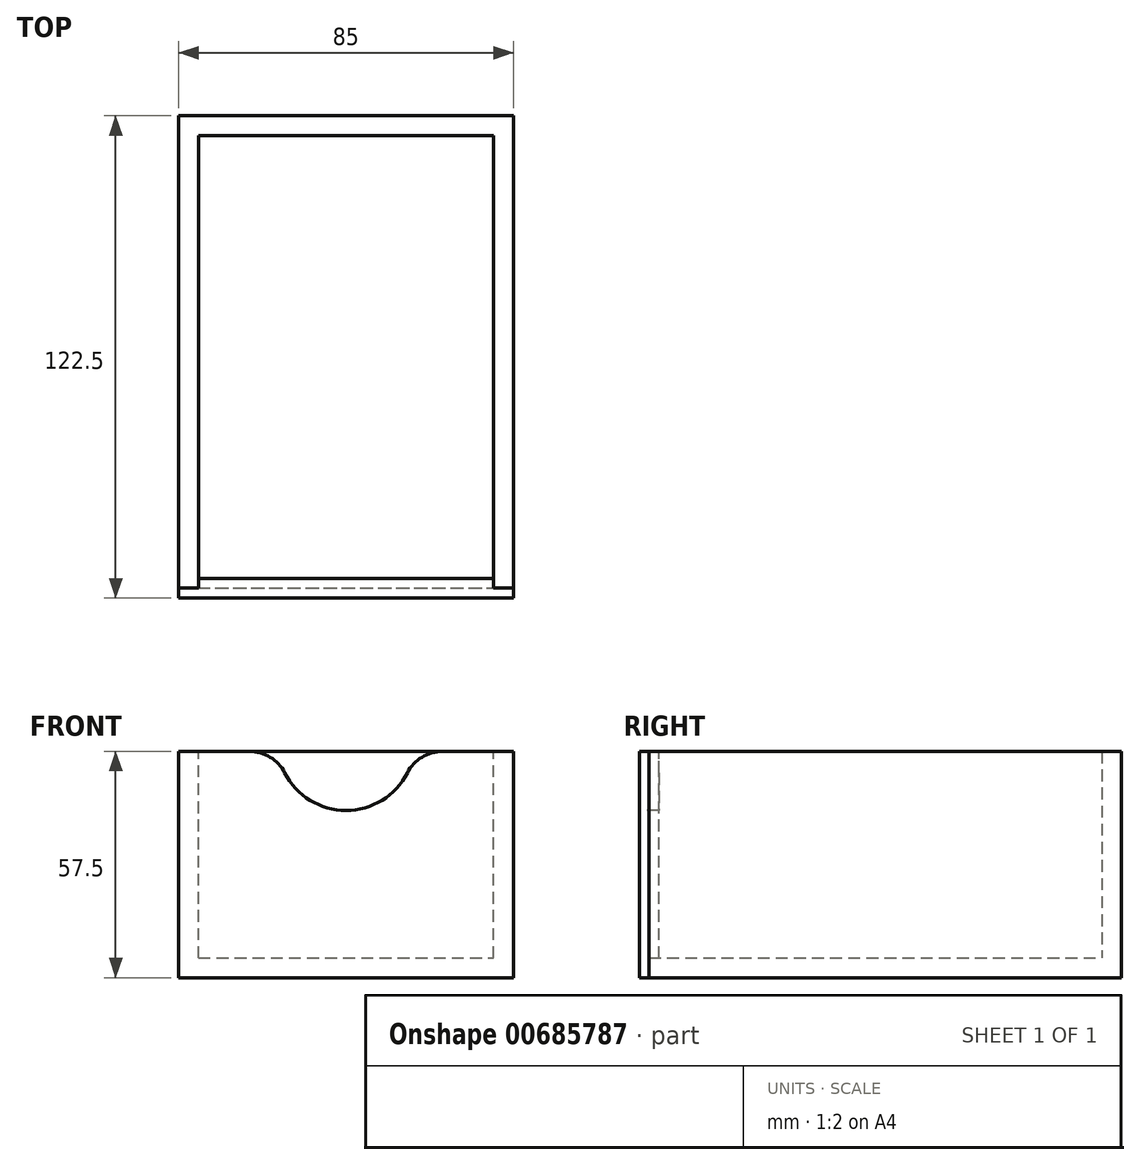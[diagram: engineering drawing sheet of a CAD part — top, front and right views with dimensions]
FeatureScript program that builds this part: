
annotation { "Feature Type Name" : "Feature", "Feature Type Description" : "" }
export const myFeature = defineFeature(function(context is Context, id is Id, definition is map)
    precondition{}
    {
        {
            var Q0;
            Q0=qCreatedBy(makeId("Front.planeOp"),FACE);
            var sketch = newSketch(context, id + "F0", { "sketchPlane" : qUnion([Q0])});
            skLineSegment(sketch, "E0.bottom", {"start": v(0, 0) * mm, "end": v(85, 0) * mm});
            skLineSegment(sketch, "E0.top", {"start": v(0, 57.5) * mm, "end": v(85, 57.5) * mm});
            skLineSegment(sketch, "E0.left", {"start": v(0, 0) * mm, "end": v(0, 57.5) * mm});
            skLineSegment(sketch, "E0.right", {"start": v(85, 0) * mm, "end": v(85, 57.5) * mm});
            skSolve(sketch);
        }
        {
            var Q0;
            Q0 = qSketchRegion(id + "F0", true);
            extrude(context, id + "F1", {"entities" : qUnion([Q0]), "depth" : 5 * mm, "offsetDistance" : 25 * mm});
        }
        {
            var Q0;
            Q0=makeQuery(id+"F0.imprint","IMPRINT",FACE,{"disambiguationData":[TD([[makeQuery(id+"F0.imprint","IMPRINT",EDGE,{"derivedFrom":sQuery(id+"F0.wireOp",EDGE,"E0.bottom")}),1.0]])]});
            var sketch = newSketch(context, id + "F2", { "sketchPlane" : qUnion([Q0])});
            skLineSegment(sketch, "E1.bottom", {"start": v(85, 0) * mm, "end": v(0, 0) * mm});
            skLineSegment(sketch, "E1.top", {"start": v(85, 5) * mm, "end": v(0, 5) * mm});
            skLineSegment(sketch, "E1.left", {"start": v(85, 0) * mm, "end": v(85, 5) * mm});
            skLineSegment(sketch, "E1.right", {"start": v(0, 0) * mm, "end": v(0, 5) * mm});
            skLineSegment(sketch, "E2.bottom", {"start": v(0, 5) * mm, "end": v(5, 5) * mm});
            skLineSegment(sketch, "E2.top", {"start": v(0, 57.62) * mm, "end": v(5, 57.62) * mm});
            skLineSegment(sketch, "E2.left", {"start": v(0, 5) * mm, "end": v(0, 57.62) * mm});
            skLineSegment(sketch, "E2.right", {"start": v(5, 5) * mm, "end": v(5, 57.62) * mm});
            skLineSegment(sketch, "E3.bottom", {"start": v(85, 5) * mm, "end": v(80, 5) * mm});
            skLineSegment(sketch, "E3.top", {"start": v(85, 57.5) * mm, "end": v(80, 57.5) * mm});
            skLineSegment(sketch, "E3.left", {"start": v(85, 5) * mm, "end": v(85, 57.5) * mm});
            skLineSegment(sketch, "E3.right", {"start": v(80, 5) * mm, "end": v(80, 57.5) * mm});
            skSolve(sketch);
        }
        {
            var Q0;
            Q0 = qSketchRegion(id + "F2", true);
            extrude(context, id + "F3", {"entities" : qUnion([Q0]), "operationType" : NewBodyOperationType.REMOVE, "depth" : 2.5 * mm, "offsetDistance" : 25 * mm});
        }
        {
            var Q0;
            Q0=makeQuery(id+"F1.opExtrude","SWEPT_FACE",FACE,{"disambiguationData":[OSD([sQuery(id+"F0.wireOp",EDGE,"E0.bottom")])]});
            var sketch = newSketch(context, id + "F4", { "sketchPlane" : qUnion([Q0])});
            skLineSegment(sketch, "E4.bottom", {"start": v(0, 2.5) * mm, "end": v(85, 2.5) * mm});
            skLineSegment(sketch, "E4.top", {"start": v(0, -115) * mm, "end": v(85, -115) * mm});
            skLineSegment(sketch, "E4.left", {"start": v(0, 2.5) * mm, "end": v(0, -115) * mm});
            skLineSegment(sketch, "E4.right", {"start": v(85, 2.5) * mm, "end": v(85, -115) * mm});
            skSolve(sketch);
        }
        {
            var Q0;
            Q0 = qSketchRegion(id + "F4", true);
            extrude(context, id + "F5", {"entities" : qUnion([Q0]), "oppositeDirection" : true, "depth" : 5 * mm, "offsetDistance" : 25 * mm});
        }
        {
            var Q0;
            Q0=makeQuery(id+"F5.opExtrude","CAP_FACE",FACE,{"disambiguationData":[OSD([sQuery(id+"F4.wireOp",EDGE,"E4.bottom"),sQuery(id+"F4.wireOp",EDGE,"E4.top"),sQuery(id+"F4.wireOp",EDGE,"E4.left"),sQuery(id+"F4.wireOp",EDGE,"E4.right")])],"isStart":false});
            var sketch = newSketch(context, id + "F6", { "sketchPlane" : qUnion([Q0])});
            skLineSegment(sketch, "E5.bottom", {"start": v(0, -2.5) * mm, "end": v(5, -2.5) * mm});
            skLineSegment(sketch, "E5.top", {"start": v(0, 115) * mm, "end": v(5, 115) * mm});
            skLineSegment(sketch, "E5.left", {"start": v(0, -2.5) * mm, "end": v(0, 115) * mm});
            skLineSegment(sketch, "E5.right", {"start": v(5, -2.5) * mm, "end": v(5, 115) * mm});
            skLineSegment(sketch, "E6.bottom", {"start": v(85, -2.5) * mm, "end": v(80, -2.5) * mm});
            skLineSegment(sketch, "E6.top", {"start": v(85, 115) * mm, "end": v(80, 115) * mm});
            skLineSegment(sketch, "E6.left", {"start": v(85, -2.5) * mm, "end": v(85, 115) * mm});
            skLineSegment(sketch, "E6.right", {"start": v(80, -2.5) * mm, "end": v(80, 115) * mm});
            skSolve(sketch);
        }
        {
            var Q0;
            Q0 = qSketchRegion(id + "F6", true);
            extrude(context, id + "F7", {"entities" : qUnion([Q0]), "operationType" : NewBodyOperationType.REMOVE, "oppositeDirection" : true, "depth" : 2.5 * mm, "offsetDistance" : 25 * mm});
        }
        {
            var Q0;
            Q0=makeQuery(id+"F5.opExtrude","SWEPT_FACE",FACE,{"disambiguationData":[OSD([sQuery(id+"F4.wireOp",EDGE,"E4.left")])]});
            var sketch = newSketch(context, id + "F8", { "sketchPlane" : qUnion([Q0])});
            skLineSegment(sketch, "E7.bottom", {"start": v(-115, 2.5) * mm, "end": v(2.5, 2.5) * mm});
            skLineSegment(sketch, "E7.top", {"start": v(-115, 57.5) * mm, "end": v(2.5, 57.5) * mm});
            skLineSegment(sketch, "E7.left", {"start": v(-115, 2.5) * mm, "end": v(-115, 57.5) * mm});
            skLineSegment(sketch, "E7.right", {"start": v(2.5, 2.5) * mm, "end": v(2.5, 57.5) * mm});
            skSolve(sketch);
        }
        {
            var Q0;
            Q0 = qSketchRegion(id + "F8", true);
            extrude(context, id + "F9", {"entities" : qUnion([Q0]), "oppositeDirection" : true, "depth" : 5 * mm, "offsetDistance" : 25 * mm});
        }
        {
            var Q0;
            Q0=makeQuery(id+"F9.opExtrude","SWEPT_BODY",BODY,{"disambiguationData":[OSD([sQuery(id+"F8.wireOp",EDGE,"E7.bottom"),sQuery(id+"F8.wireOp",EDGE,"E7.top"),sQuery(id+"F8.wireOp",EDGE,"E7.left"),sQuery(id+"F8.wireOp",EDGE,"E7.right")])]});
            transform(context, id + "F10", {"entities" : qUnion([Q0]), "transformType" : TransformType.TRANSLATION_3D, "dx" : 80 * mm, "dy" : 0 * mm, "dz" : 0 * mm, "makeCopy" : true});
        }
        {
            var Q0;
            Q0=makeQuery(id+"F5.opExtrude","SWEPT_FACE",FACE,{"disambiguationData":[OSD([sQuery(id+"F4.wireOp",EDGE,"E4.top")])]});
            var sketch = newSketch(context, id + "F11", { "sketchPlane" : qUnion([Q0])});
            skLineSegment(sketch, "E8.bottom", {"start": v(-85, 0) * mm, "end": v(0, 0) * mm});
            skLineSegment(sketch, "E8.top", {"start": v(-85, 57.5) * mm, "end": v(0, 57.5) * mm});
            skLineSegment(sketch, "E8.left", {"start": v(-85, 0) * mm, "end": v(-85, 57.5) * mm});
            skLineSegment(sketch, "E8.right", {"start": v(0, 0) * mm, "end": v(0, 57.5) * mm});
            skSolve(sketch);
        }
        {
            var Q0;
            Q0 = qSketchRegion(id + "F11", true);
            extrude(context, id + "F12", {"entities" : qUnion([Q0]), "depth" : 2.5 * mm, "offsetDistance" : 25 * mm});
        }
        {
            var Q0;
            Q0=makeQuery(id+"F12.opExtrude","CAP_FACE",FACE,{"disambiguationData":[OSD([sQuery(id+"F11.wireOp",EDGE,"E8.bottom"),sQuery(id+"F11.wireOp",EDGE,"E8.top"),sQuery(id+"F11.wireOp",EDGE,"E8.left"),sQuery(id+"F11.wireOp",EDGE,"E8.right")])],"isStart":true});
            var sketch = newSketch(context, id + "F13", { "sketchPlane" : qUnion([Q0])});
            skLineSegment(sketch, "E9.bottom", {"start": v(5, 57.5) * mm, "end": v(80, 57.5) * mm});
            skLineSegment(sketch, "E9.top", {"start": v(5, 5) * mm, "end": v(80, 5) * mm});
            skLineSegment(sketch, "E9.left", {"start": v(5, 57.5) * mm, "end": v(5, 5) * mm});
            skLineSegment(sketch, "E9.right", {"start": v(80, 57.5) * mm, "end": v(80, 5) * mm});
            skSolve(sketch);
        }
        {
            var Q0;
            Q0 = qSketchRegion(id + "F13", true);
            extrude(context, id + "F14", {"entities" : qUnion([Q0]), "operationType" : NewBodyOperationType.ADD, "depth" : 2.5 * mm, "offsetDistance" : 25 * mm});
        }
        {
            var Q0;
            Q0=makeQuery(id+"F1.opExtrude","CAP_FACE",FACE,{"disambiguationData":[OSD([sQuery(id+"F0.wireOp",EDGE,"E0.bottom"),sQuery(id+"F0.wireOp",EDGE,"E0.top"),sQuery(id+"F0.wireOp",EDGE,"E0.left"),sQuery(id+"F0.wireOp",EDGE,"E0.right")])],"isStart":false});
            var sketch = newSketch(context, id + "F15", { "sketchPlane" : qUnion([Q0])});
            skCircle(sketch, "E10", {"center": v(42.5, 60) * mm, "radius": 17.5 * mm});
            skPoint(sketch, "E10.centerSnap0", {"position": v(42.5, 57.5) * mm});
            skLineSegment(sketch, "E11", {"start": v(42.5, 57.5) * mm, "end": v(42.5, 60) * mm, "construction": true});
            skSolve(sketch);
        }
        {
            var Q0;
            Q0 = qSketchRegion(id + "F15", true);
            extrude(context, id + "F16", {"entities" : qUnion([Q0]), "operationType" : NewBodyOperationType.REMOVE, "oppositeDirection" : true, "depth" : 25 * mm, "offsetDistance" : 25 * mm});
        }
        {
            var Q0;
            Q0=makeQuery(id+"F16.boolean.opBoolean","INTERSECT",EDGE,{"disambiguationData":[OD(1.0)],"derivedFrom":[makeQuery(id+"F1.opExtrude","SWEPT_FACE",FACE,{"disambiguationData":[OSD([sQuery(id+"F0.wireOp",EDGE,"E0.top")])]}),makeQuery(id+"F16.opExtrude","SWEPT_FACE",FACE,{"disambiguationData":[OSD([sQuery(id+"F15.wireOp",EDGE,"E10")])]})]});
            var Q1;
            Q1=makeQuery(id+"F16.boolean.opBoolean","INTERSECT",EDGE,{"disambiguationData":[OD(0.0)],"derivedFrom":[makeQuery(id+"F1.opExtrude","SWEPT_FACE",FACE,{"disambiguationData":[OSD([sQuery(id+"F0.wireOp",EDGE,"E0.top")])]}),makeQuery(id+"F16.opExtrude","SWEPT_FACE",FACE,{"disambiguationData":[OSD([sQuery(id+"F15.wireOp",EDGE,"E10")])]})]});
            fillet(context, id + "F17", {"entities" : qUnion([Q0, Q1]), "radius" : 10 * mm, "tangentPropagation" : true, "allowEdgeOverflow" : false});
        }
    });
